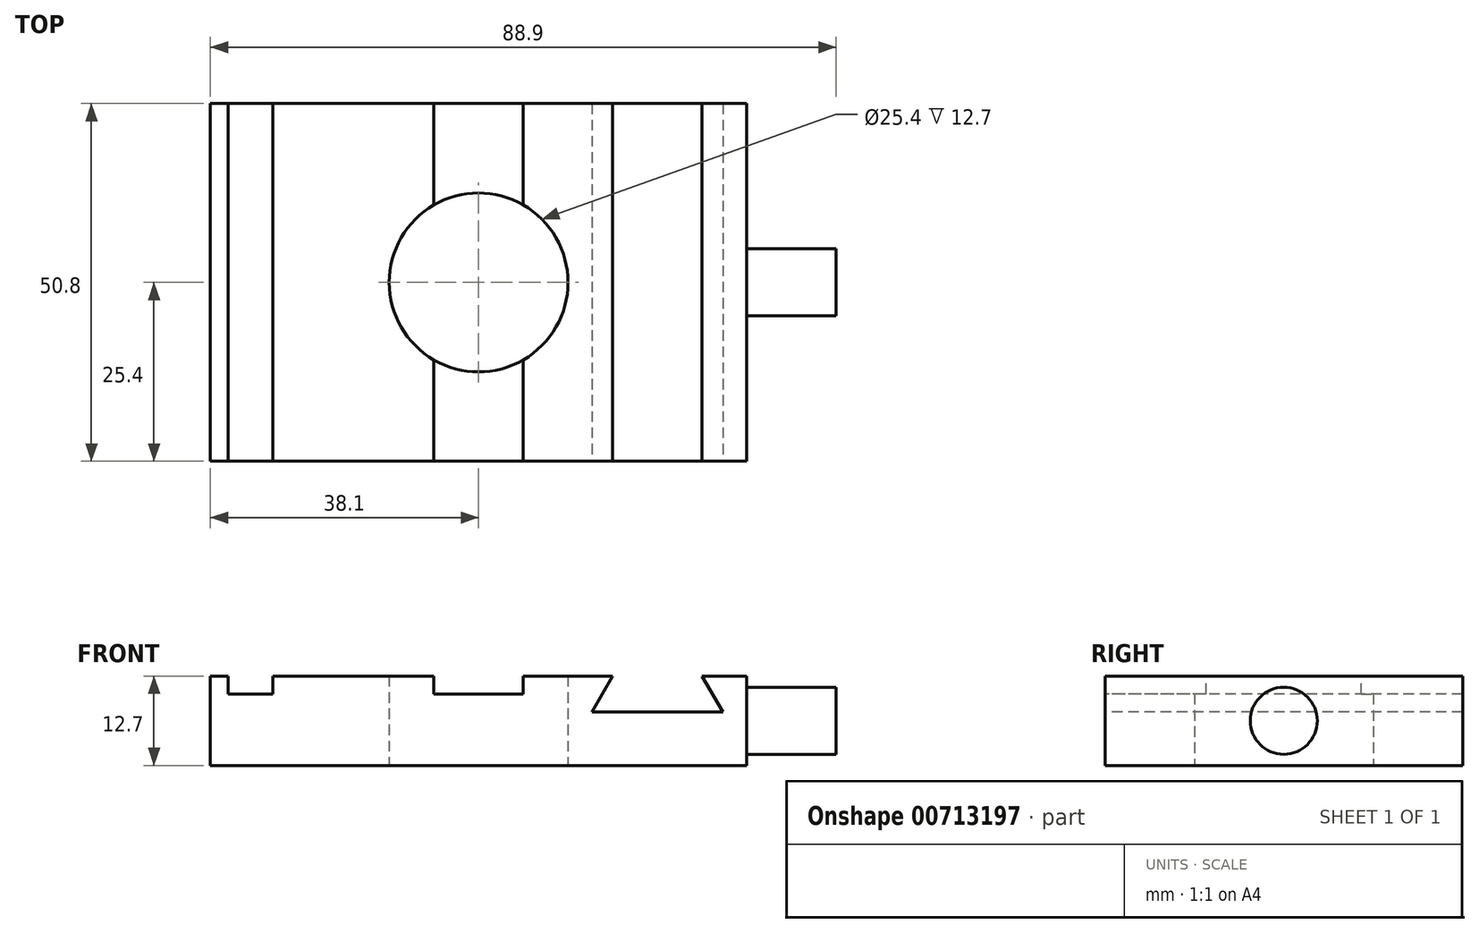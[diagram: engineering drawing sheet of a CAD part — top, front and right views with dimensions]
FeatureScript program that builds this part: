
annotation { "Feature Type Name" : "Feature", "Feature Type Description" : "" }
export const myFeature = defineFeature(function(context is Context, id is Id, definition is map)
    precondition{}
    {
        {
            var Q0;
            Q0=qCreatedBy(makeId("Top.planeOp"),FACE);
            var sketch = newSketch(context, id + "F0", { "sketchPlane" : qUnion([Q0])});
            skLineSegment(sketch, "E0.bottom", {"start": v(38.1, -25.4) * mm, "end": v(-38.1, -25.4) * mm});
            skLineSegment(sketch, "E0.top", {"start": v(38.1, 25.4) * mm, "end": v(-38.1, 25.4) * mm});
            skLineSegment(sketch, "E0.left", {"start": v(38.1, -25.4) * mm, "end": v(38.1, 25.4) * mm});
            skLineSegment(sketch, "E0.right", {"start": v(-38.1, -25.4) * mm, "end": v(-38.1, 25.4) * mm});
            skPoint(sketch, "E0.middle", {"position": v(0, 0) * mm});
            skCircle(sketch, "E1", {"center": v(0, 0) * mm, "radius": 12.7 * mm});
            skSolve(sketch);
        }
        {
            var Q0;
            Q0=makeQuery(id+"F0.imprint","IMPRINT",FACE,{"disambiguationData":[TD([[makeQuery(id+"F0.imprint","IMPRINT",EDGE,{"derivedFrom":sQuery(id+"F0.wireOp",EDGE,"E0.bottom")}),-1.0]])]});
            extrude(context, id + "F1", {"entities" : qUnion([Q0]), "depth" : 12.7 * mm, "offsetDistance" : 25.4 * mm});
        }
        {
            var Q0;
            Q0=makeQuery(id+"F1.opExtrude","CAP_FACE",FACE,{"disambiguationData":[OSD([sQuery(id+"F0.wireOp",EDGE,"E0.bottom"),sQuery(id+"F0.wireOp",EDGE,"E0.top"),sQuery(id+"F0.wireOp",EDGE,"E0.left"),sQuery(id+"F0.wireOp",EDGE,"E0.right"),sQuery(id+"F0.wireOp",EDGE,"E1")])],"isStart":false});
            var sketch = newSketch(context, id + "F2", { "sketchPlane" : qUnion([Q0])});
            skLineSegment(sketch, "E2.bottom", {"start": v(-35.56, 25.4) * mm, "end": v(-29.21, 25.4) * mm});
            skLineSegment(sketch, "E2.top", {"start": v(-35.56, -25.4) * mm, "end": v(-29.21, -25.4) * mm});
            skLineSegment(sketch, "E2.left", {"start": v(-35.56, 25.4) * mm, "end": v(-35.56, -25.4) * mm});
            skLineSegment(sketch, "E2.right", {"start": v(-29.21, 25.4) * mm, "end": v(-29.21, -25.4) * mm});
            skLineSegment(sketch, "E3", {"start": v(-6.35, 25.4) * mm, "end": v(-6.35, -25.4) * mm});
            skLineSegment(sketch, "E4", {"start": v(-6.35, -25.4) * mm, "end": v(6.35, -25.4) * mm});
            skLineSegment(sketch, "E5", {"start": v(6.35, -25.4) * mm, "end": v(6.35, 25.4) * mm});
            skLineSegment(sketch, "E6", {"start": v(6.35, 25.4) * mm, "end": v(-6.35, 25.4) * mm});
            skPoint(sketch, "E7", {"position": v(0, 0) * mm});
            skLineSegment(sketch, "E8", {"start": v(0, 25.4) * mm, "end": v(0, -25.4) * mm, "construction": true});
            skSolve(sketch);
        }
        {
            var Q0;
            Q0=makeQuery(id+"F2.imprint","IMPRINT",FACE,{"disambiguationData":[TD([[makeQuery(id+"F2.imprint","IMPRINT",EDGE,{"derivedFrom":sQuery(id+"F2.wireOp",EDGE,"E2.bottom")}),1.0]])]});
            var Q1;
            {var subQ0=sQuery(id+"F2.wireOp",EDGE,"E4");Q1=makeQuery(id+"F2.imprint","IMPRINT",FACE,{"disambiguationData":[TD([[makeQuery(id+"F2.imprint","IMPRINT",EDGE,{"derivedFrom":subQ0}),-1.0]])]});}
            var Q2;
            {var subQ0=sQuery(id+"F2.wireOp",EDGE,"E6");Q2=makeQuery(id+"F2.imprint","IMPRINT",FACE,{"disambiguationData":[TD([[makeQuery(id+"F2.imprint","IMPRINT",EDGE,{"derivedFrom":subQ0}),1.0]])]});}
            extrude(context, id + "F3", {"entities" : qUnion([Q0, Q1, Q2]), "operationType" : NewBodyOperationType.REMOVE, "oppositeDirection" : true, "depth" : 2.54 * mm, "offsetDistance" : 25.4 * mm});
        }
        {
            var Q0;
            Q0=makeQuery(id+"F1.opExtrude","SWEPT_FACE",FACE,{"disambiguationData":[OSD([sQuery(id+"F0.wireOp",EDGE,"E0.bottom")])]});
            var sketch = newSketch(context, id + "F4", { "sketchPlane" : qUnion([Q0])});
            skLineSegment(sketch, "E9", {"start": v(19.05, 12.7) * mm, "end": v(16.12, 7.62) * mm});
            skLineSegment(sketch, "E10", {"start": v(16.12, 7.62) * mm, "end": v(34.68, 7.62) * mm});
            skLineSegment(sketch, "E11", {"start": v(34.68, 7.62) * mm, "end": v(31.75, 12.7) * mm});
            skLineSegment(sketch, "E12", {"start": v(31.75, 12.7) * mm, "end": v(19.05, 12.7) * mm});
            skLineSegment(sketch, "E13", {"start": v(25.4, 12.7) * mm, "end": v(25.4, 7.62) * mm, "construction": true});
            skSolve(sketch);
        }
        {
            var Q0;
            Q0=makeQuery(id+"F4.imprint","IMPRINT",FACE,{"disambiguationData":[TD([[makeQuery(id+"F4.imprint","IMPRINT",EDGE,{"derivedFrom":sQuery(id+"F4.wireOp",EDGE,"E9")}),1.0]])]});
            extrude(context, id + "F5", {"entities" : qUnion([Q0]), "operationType" : NewBodyOperationType.REMOVE, "endBound" : BoundingType.THROUGH_ALL, "oppositeDirection" : true, "depth" : 25.4 * mm, "offsetDistance" : 25.4 * mm});
        }
        {
            var Q0;
            Q0=makeQuery(id+"F1.opExtrude","SWEPT_FACE",FACE,{"disambiguationData":[OSD([sQuery(id+"F0.wireOp",EDGE,"E0.left")])]});
            var sketch = newSketch(context, id + "F6", { "sketchPlane" : qUnion([Q0])});
            skCircle(sketch, "E14", {"center": v(0, 6.35) * mm, "radius": 4.76 * mm});
            skPoint(sketch, "E14.centerSnap0", {"position": v(-25.4, 6.35) * mm});
            skPoint(sketch, "E14.centerSnap1", {"position": v(0, 12.7) * mm});
            skSolve(sketch);
        }
        {
            var Q0;
            Q0=makeQuery(id+"F6.imprint","IMPRINT",FACE,{"disambiguationData":[TD([[makeQuery(id+"F6.imprint","IMPRINT",EDGE,{"derivedFrom":sQuery(id+"F6.wireOp",EDGE,"E14")}),1.0]])]});
            var Q1;
            Q1=sQuery(id+"F6.wireOp",EDGE,"E14");
            extrude(context, id + "F7", {"entities" : qUnion([Q0]), "operationType" : NewBodyOperationType.ADD, "surfaceOperationType" : NewSurfaceOperationType.ADD, "surfaceEntities" : qUnion([Q1]), "depth" : 12.7 * mm, "offsetDistance" : 25.4 * mm});
        }
    });
